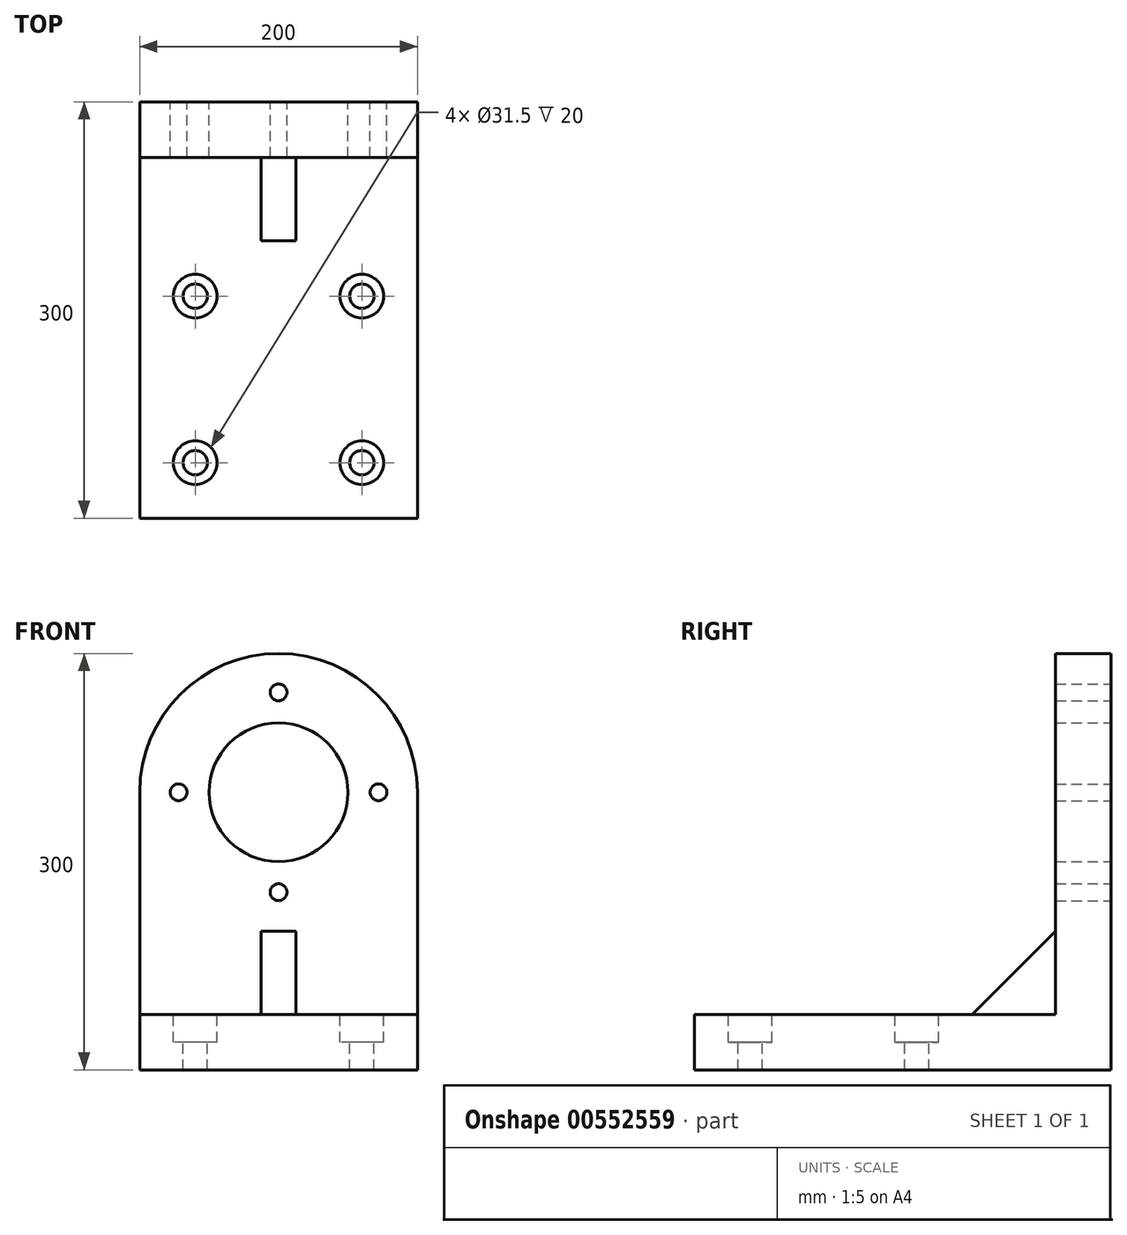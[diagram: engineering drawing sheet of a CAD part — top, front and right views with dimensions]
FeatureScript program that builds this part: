
annotation { "Feature Type Name" : "Feature", "Feature Type Description" : "" }
export const myFeature = defineFeature(function(context is Context, id is Id, definition is map)
    precondition{}
    {
        {
            var Q0;
            Q0=qCreatedBy(makeId("Front.planeOp"),FACE);
            var sketch = newSketch(context, id + "F0", { "sketchPlane" : qUnion([Q0])});
            skCircle(sketch, "E0", {"center": v(0, 0) * mm, "radius": 72 * mm, "construction": true});
            skCircle(sketch, "E1", {"center": v(0, 0) * mm, "radius": 100 * mm});
            skLineSegment(sketch, "E2", {"start": v(-100, 0) * mm, "end": v(-100, -200) * mm});
            skLineSegment(sketch, "E3", {"start": v(100, 0) * mm, "end": v(100, -200) * mm});
            skLineSegment(sketch, "E4", {"start": v(-100, -200) * mm, "end": v(100, -200) * mm});
            skCircle(sketch, "E5", {"center": v(0, 0) * mm, "radius": 50 * mm});
            skLineSegment(sketch, "E6", {"start": v(-100, 0) * mm, "end": v(100, 0) * mm, "construction": true});
            skLineSegment(sketch, "E7", {"start": v(0, -100) * mm, "end": v(0, 100) * mm, "construction": true});
            skCircle(sketch, "E8", {"center": v(0, 72) * mm, "radius": 7 * mm});
            skCircle(sketch, "E9", {"center": v(0, -72) * mm, "radius": 7 * mm});
            skCircle(sketch, "E10", {"center": v(-72, 0) * mm, "radius": 7 * mm});
            skCircle(sketch, "E11", {"center": v(72, 0) * mm, "radius": 7 * mm});
            skLineSegment(sketch, "E12", {"start": v(-100, -160) * mm, "end": v(100, -160) * mm});
            skSolve(sketch);
        }
        {
            var Q0;
            Q0 = qSketchRegion(id + "F0", true);
            var Q1;
            Q1=makeQuery(id+"F0.imprint","IMPRINT",FACE,{"disambiguationData":[TD([[makeQuery(id+"F0.imprint","IMPRINT",EDGE,{"derivedFrom":sQuery(id+"F0.wireOp",EDGE,"E8")}),1.0]])]});
            var Q2;
            Q2=makeQuery(id+"F0.imprint","IMPRINT",FACE,{"disambiguationData":[TD([[makeQuery(id+"F0.imprint","IMPRINT",EDGE,{"derivedFrom":sQuery(id+"F0.wireOp",EDGE,"E11")}),1.0]])]});
            var Q3;
            Q3=makeQuery(id+"F0.imprint","IMPRINT",FACE,{"disambiguationData":[TD([[makeQuery(id+"F0.imprint","IMPRINT",EDGE,{"derivedFrom":sQuery(id+"F0.wireOp",EDGE,"E9")}),1.0]])]});
            var Q4;
            Q4=makeQuery(id+"F0.imprint","IMPRINT",FACE,{"disambiguationData":[TD([[makeQuery(id+"F0.imprint","IMPRINT",EDGE,{"derivedFrom":sQuery(id+"F0.wireOp",EDGE,"E10")}),1.0]])]});
            extrude(context, id + "F1", {"entities" : qUnion([Q0, Q1, Q2, Q3, Q4]), "depth" : 40 * mm, "offsetDistance" : 25 * mm});
        }
        {
            var Q0;
            Q0=sQuery(id+"F0.wireOp",VERTEX,"E10.center");
            var Q1;
            Q1=sQuery(id+"F0.wireOp",VERTEX,"E9.center");
            var Q2;
            Q2=sQuery(id+"F0.wireOp",VERTEX,"E11.center");
            var Q3;
            Q3=sQuery(id+"F0.wireOp",VERTEX,"E8.center");
            var Q4;
            Q4=makeQuery(id+"F1.opExtrude","SWEPT_BODY",BODY,{"disambiguationData":[OSD([sQuery(id+"F0.wireOp",EDGE,"E1"),sQuery(id+"F0.wireOp",EDGE,"E2"),sQuery(id+"F0.wireOp",EDGE,"E3"),sQuery(id+"F0.wireOp",EDGE,"E4"),sQuery(id+"F0.wireOp",EDGE,"E5")])]});
            hole(context, id + "F2", {"style" : HoleStyle.SIMPLE, "endStyle" : HoleEndStyle.THROUGH, "oppositeDirection" : true, "standardTappedOrClearance" : lookupTablePath({ "standard" : "ISO", "engagement" : "75%", "pitch" : "2 mm", "size" : "M14", "type" : "Tapped" }), "standardBlindInLast" : lookupTablePath({ "standard" : "ISO", "engagement" : "75%", "pitch" : "2 mm", "size" : "M14", "type" : "Tapped" }), "holeDiameter" : 12.1 * mm, "showTappedDepth" : true, "isTappedThrough" : true, "tappedDepth" : 12 * mm, "tapClearance" : 3, "locations" : qUnion([Q0, Q1, Q2, Q3]), "scope" : qUnion([Q4]), "majorDiameter" : 14 * mm});
        }
        {
            var Q0;
            {var subQ0=sQuery(id+"F0.wireOp",EDGE,"E4");Q0=makeQuery(id+"F0.imprint","IMPRINT",FACE,{"disambiguationData":[TD([[makeQuery(id+"F0.imprint","IMPRINT",EDGE,{"derivedFrom":subQ0}),1.0]])]});}
            extrude(context, id + "F3", {"entities" : qUnion([Q0]), "operationType" : NewBodyOperationType.ADD, "depth" : 300 * mm, "offsetDistance" : 25 * mm});
        }
        {
            var Q0;
            Q0=makeQuery(id+"F3.opExtrude","SWEPT_FACE",FACE,{"disambiguationData":[OSD([sQuery(id+"F0.wireOp",EDGE,"E12")])]});
            var sketch = newSketch(context, id + "F4", { "sketchPlane" : qUnion([Q0])});
            skPoint(sketch, "E13", {"position": v(60, -260) * mm});
            skPoint(sketch, "E14.0.1.0", {"position": v(60, -140) * mm});
            skPoint(sketch, "E14.1.0.0", {"position": v(-60, -260) * mm});
            skPoint(sketch, "E14.1.1.0", {"position": v(-60, -140) * mm});
            skLineSegment(sketch, "E14.direction1", {"start": v(60, -260) * mm, "end": v(-60, -260) * mm, "construction": true});
            skLineSegment(sketch, "E14.direction2", {"start": v(60, -260) * mm, "end": v(60, -140) * mm, "construction": true});
            skSolve(sketch);
        }
        {
            var Q0;
            Q0=sQuery(id+"F4.wireOp",VERTEX,"E13");
            var Q1;
            Q1=sQuery(id+"F4.wireOp",VERTEX,"E14.1.0.0");
            var Q2;
            Q2=sQuery(id+"F4.wireOp",VERTEX,"E14.0.1.0");
            var Q3;
            Q3=sQuery(id+"F4.wireOp",VERTEX,"E14.1.1.0");
            var Q4;
            Q4=makeQuery(id+"F1.opExtrude","SWEPT_BODY",BODY,{"disambiguationData":[OSD([sQuery(id+"F0.wireOp",EDGE,"E1"),sQuery(id+"F0.wireOp",EDGE,"E2"),sQuery(id+"F0.wireOp",EDGE,"E3"),sQuery(id+"F0.wireOp",EDGE,"E4"),sQuery(id+"F0.wireOp",EDGE,"E5")])]});
            hole(context, id + "F5", {"style" : HoleStyle.C_BORE, "endStyle" : HoleEndStyle.THROUGH, "holeDiameter" : 17.5 * mm, "cBoreDiameter" : 31.5 * mm, "cBoreDepth" : 20 * mm, "isTappedThrough" : true, "tappedDepth" : 12 * mm, "tapClearance" : 3, "locations" : qUnion([Q0, Q1, Q2, Q3]), "scope" : qUnion([Q4])});
        }
        {
            var Q0;
            Q0=qCreatedBy(makeId("Right.planeOp"),FACE);
            var sketch = newSketch(context, id + "F6", { "sketchPlane" : qUnion([Q0])});
            skLineSegment(sketch, "E15.0", {"start": v(-40, 0) * mm, "end": v(-40, -160) * mm});
            skLineSegment(sketch, "E16.0", {"start": v(-300, -160) * mm, "end": v(-40, -160) * mm});
            skLineSegment(sketch, "E17", {"start": v(-100, -160) * mm, "end": v(-40, -100) * mm});
            skSolve(sketch);
        }
        {
            var Q0;
            {var subQ3=sQuery(id+"F6.wireOp",EDGE,"E17");Q0=makeQuery(id+"F6.imprint","IMPRINT",FACE,{"disambiguationData":[TD([[makeQuery(id+"F6.imprint","IMPRINT",EDGE,{"derivedFrom":subQ3}),-1.0]])]});}
            extrude(context, id + "F7", {"entities" : qUnion([Q0]), "operationType" : NewBodyOperationType.ADD, "endBound" : BoundingType.SYMMETRIC, "depth" : 25 * mm, "offsetDistance" : 25 * mm});
        }
    });
